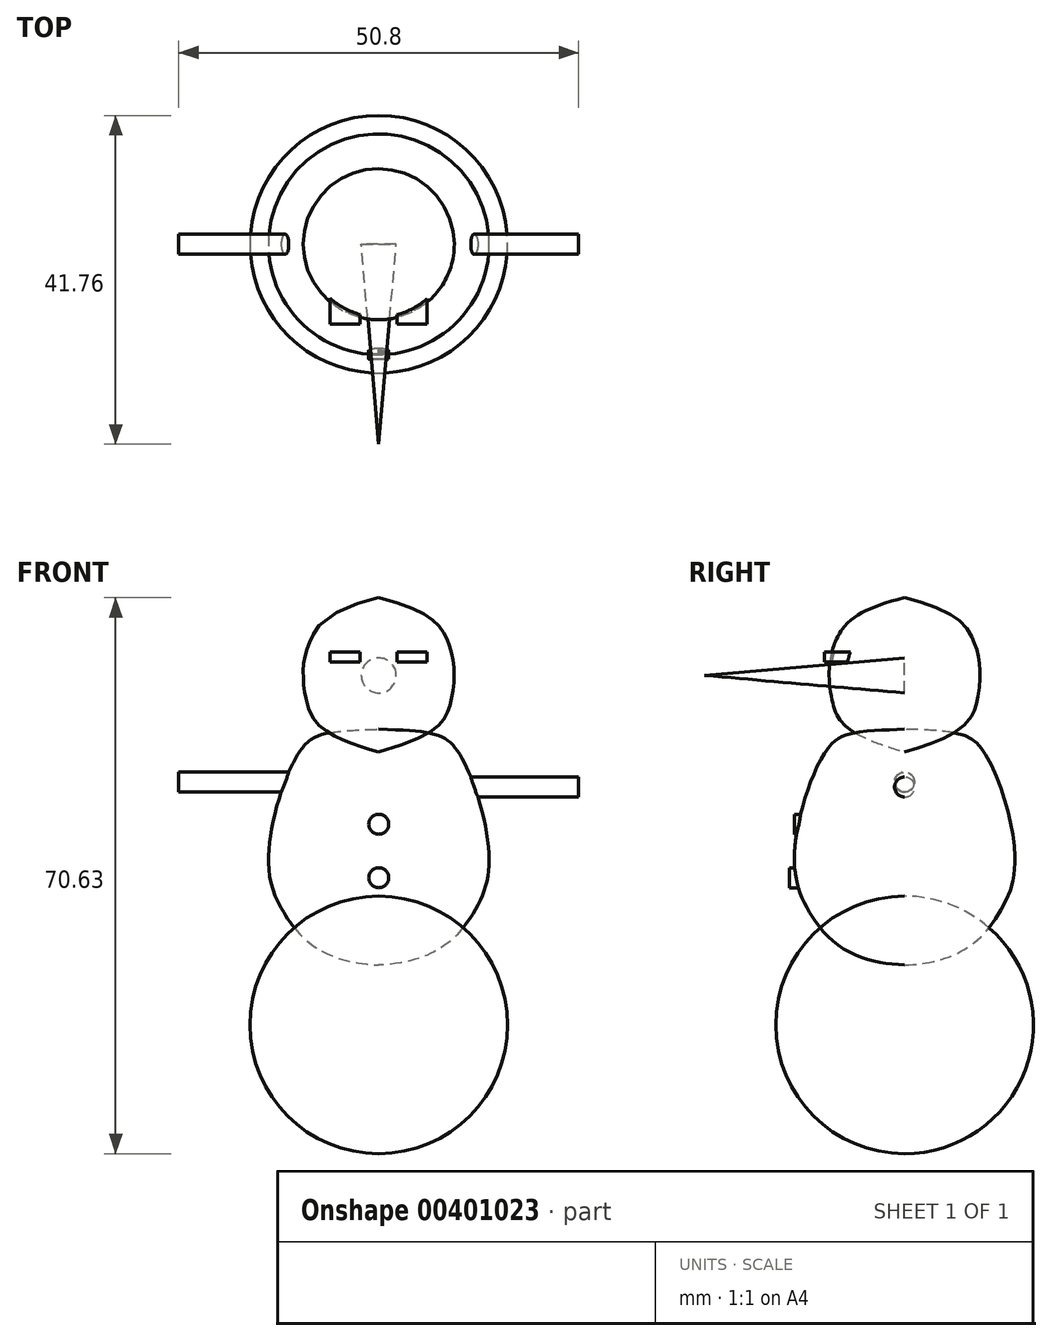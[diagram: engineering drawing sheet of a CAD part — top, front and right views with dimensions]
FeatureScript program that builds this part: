
annotation { "Feature Type Name" : "Feature", "Feature Type Description" : "" }
export const myFeature = defineFeature(function(context is Context, id is Id, definition is map)
    precondition{}
    {
        {
            var Q0;
            Q0=qCreatedBy(makeId("Front.planeOp"),FACE);
            var sketch = newSketch(context, id + "F0", { "sketchPlane" : qUnion([Q0])});
            skFitSpline(sketch, "E0", {"points": [v(0, 2.89) * mm, v(10.07, 0) * mm, v(14, -12.83) * mm, v(12.03, -20.44) * mm, v(0, -27.07) * mm], "startDerivative": vector(82.95, -3.07) * mm, "endDerivative": vector(-79.02, -2.93) * mm});
            skLineSegment(sketch, "E1", {"start": v(0, 54.46) * mm, "end": v(0, -50.15) * mm});
            skSolve(sketch);
        }
        {
            var Q0;
            {var subQ0=sQuery(id+"F0.wireOp",EDGE,"E0");Q0=makeQuery(id+"F0.imprint","IMPRINT",FACE,{"disambiguationData":[TD([[makeQuery(id+"F0.imprint","IMPRINT",EDGE,{"derivedFrom":subQ0}),-1.0]])]});}
            var Q1;
            Q1=sQuery(id+"F0.wireOp",EDGE,"E1");
            revolve(context, id + "F1", {"entities" : qUnion([Q0]), "axis" : qUnion([Q1]), "revolveType" : RevolveType.FULL});
        }
        {
            var Q0;
            Q0=qCreatedBy(makeId("Front.planeOp"),FACE);
            var sketch = newSketch(context, id + "F2", { "sketchPlane" : qUnion([Q0])});
            skLineSegment(sketch, "E2", {"start": v(0, 95.14) * mm, "end": v(0, -94.77) * mm});
            skFitSpline(sketch, "E3", {"points": [v(0, 19.59) * mm, v(8.6, 14.43) * mm, v(9.58, 10.5) * mm, v(9.09, 6.08) * mm, v(0, 0) * mm], "startDerivative": vector(61.63, -14.8) * mm, "endDerivative": vector(-73.17, -20.68) * mm});
            skSolve(sketch);
        }
        {
            var Q0;
            {var subQ0=sQuery(id+"F2.wireOp",EDGE,"E3");Q0=makeQuery(id+"F2.imprint","IMPRINT",FACE,{"disambiguationData":[TD([[makeQuery(id+"F2.imprint","IMPRINT",EDGE,{"derivedFrom":subQ0}),-1.0]])]});}
            var Q1;
            Q1=sQuery(id+"F2.wireOp",EDGE,"E2");
            revolve(context, id + "F3", {"entities" : qUnion([Q0]), "axis" : qUnion([Q1]), "revolveType" : RevolveType.FULL});
        }
        {
            var Q0;
            Q0=qCreatedBy(makeId("Front.planeOp"),FACE);
            var sketch = newSketch(context, id + "F4", { "sketchPlane" : qUnion([Q0])});
            skLineSegment(sketch, "E4", {"start": v(0, 39.72) * mm, "end": v(0, -72.26) * mm});
            skArc(sketch, "E5", {"start": v(0, -51.04) * mm, "mid": v(16.36, -34.68) * mm, "end": v(0, -18.33) * mm});
            skSolve(sketch);
        }
        {
            var Q0;
            {var subQ0=sQuery(id+"F4.wireOp",EDGE,"e939705f-58e8-430a-9148-d6e31caf1298");var subQ1=sQuery(id+"F4.wireOp",EDGE,"E4");var subQ2=makeQuery(id+"F4.imprint","INTERSECT",VERTEX,{"disambiguationData":[OD(0.0)],"derivedFrom":[subQ1,subQ0]});Q0=makeQuery(id+"F4.imprint","IMPRINT",FACE,{"disambiguationData":[TD([[makeQuery(id+"F4.imprint","IMPRINT",EDGE,{"disambiguationData":[TD([[subQ2,-1.0]])],"derivedFrom":subQ1}),1.0]])]});}
            var Q1;
            {var subQ0=sQuery(id+"F4.wireOp",EDGE,"E5");Q1=makeQuery(id+"F4.imprint","IMPRINT",FACE,{"disambiguationData":[TD([[makeQuery(id+"F4.imprint","IMPRINT",EDGE,{"derivedFrom":subQ0}),1.0]])]});}
            var Q2;
            Q2=sQuery(id+"F4.wireOp",EDGE,"E4");
            revolve(context, id + "F5", {"entities" : qUnion([Q0, Q1]), "axis" : qUnion([Q2]), "revolveType" : RevolveType.FULL});
        }
        {
            var Q0;
            Q0=qCreatedBy(makeId("Front.planeOp"),FACE);
            var sketch = newSketch(context, id + "F6", { "sketchPlane" : qUnion([Q0])});
            skLineSegment(sketch, "E6.bottom", {"start": v(-6.17, 12.7) * mm, "end": v(-2.36, 12.7) * mm});
            skLineSegment(sketch, "E6.top", {"start": v(-6.17, 11.43) * mm, "end": v(-2.36, 11.43) * mm});
            skLineSegment(sketch, "E6.left", {"start": v(-6.17, 12.7) * mm, "end": v(-6.17, 11.43) * mm});
            skLineSegment(sketch, "E6.right", {"start": v(-2.36, 12.7) * mm, "end": v(-2.36, 11.43) * mm});
            skSolve(sketch);
        }
        {
            var Q0;
            Q0 = qSketchRegion(id + "F6", true);
            extrude(context, id + "F7", {"entities" : qUnion([Q0]), "operationType" : NewBodyOperationType.ADD, "depth" : 10.16 * mm});
        }
        {
            var Q0;
            Q0=qCreatedBy(makeId("Front.planeOp"),FACE);
            var sketch = newSketch(context, id + "F8", { "sketchPlane" : qUnion([Q0])});
            skLineSegment(sketch, "E7.bottom", {"start": v(2.34, 12.67) * mm, "end": v(6.15, 12.67) * mm});
            skLineSegment(sketch, "E7.top", {"start": v(2.34, 11.4) * mm, "end": v(6.15, 11.4) * mm});
            skLineSegment(sketch, "E7.left", {"start": v(2.34, 12.67) * mm, "end": v(2.34, 11.4) * mm});
            skLineSegment(sketch, "E7.right", {"start": v(6.15, 12.67) * mm, "end": v(6.15, 11.4) * mm});
            skSolve(sketch);
        }
        {
            var Q0;
            Q0 = qSketchRegion(id + "F8", true);
            extrude(context, id + "F9", {"entities" : qUnion([Q0]), "operationType" : NewBodyOperationType.ADD, "depth" : 10.16 * mm});
        }
        {
            var Q0;
            Q0=qCreatedBy(makeId("Front.planeOp"),FACE);
            var sketch = newSketch(context, id + "F10", { "sketchPlane" : qUnion([Q0])});
            skCircle(sketch, "E8", {"center": v(0, 9.71) * mm, "radius": 2.22 * mm});
            skSolve(sketch);
        }
        {
            var Q0;
            Q0 = qSketchRegion(id + "F10", true);
            extrude(context, id + "F11", {"entities" : qUnion([Q0]), "depth" : 27.13 * mm, "hasDraft" : true, "draftAngle" : 5 * degree, "draftPullDirection" : true});
        }
        {
            var Q0;
            Q0=qCreatedBy(makeId("Right.planeOp"),FACE);
            var sketch = newSketch(context, id + "F12", { "sketchPlane" : qUnion([Q0])});
            skCircle(sketch, "E9", {"center": v(0, -4.47) * mm, "radius": 1.27 * mm});
            skSolve(sketch);
        }
        {
            var Q0;
            Q0 = qSketchRegion(id + "F12", true);
            var Q1;
            Q1 = qSketchRegion(id + "F14", true);
            extrude(context, id + "F13", {"entities" : qUnion([Q0, Q1]), "operationType" : NewBodyOperationType.ADD, "depth" : 25.4 * mm});
        }
        {
            var Q0;
            Q0=qCreatedBy(makeId("Right.planeOp"),FACE);
            var sketch = newSketch(context, id + "F14", { "sketchPlane" : qUnion([Q0])});
            skCircle(sketch, "E10", {"center": v(0, -3.85) * mm, "radius": 1.27 * mm});
            skSolve(sketch);
        }
        {
            var Q0;
            Q0 = qSketchRegion(id + "F14", true);
            extrude(context, id + "F15", {"entities" : qUnion([Q0]), "operationType" : NewBodyOperationType.ADD, "oppositeDirection" : true, "depth" : 25.4 * mm});
        }
        {
            var Q0;
            Q0=qCreatedBy(makeId("Front.planeOp"),FACE);
            var sketch = newSketch(context, id + "F16", { "sketchPlane" : qUnion([Q0])});
            skCircle(sketch, "E11", {"center": v(0, -9.19) * mm, "radius": 1.27 * mm});
            skSolve(sketch);
        }
        {
            var Q0;
            Q0 = qSketchRegion(id + "F16", true);
            extrude(context, id + "F17", {"entities" : qUnion([Q0]), "operationType" : NewBodyOperationType.ADD, "depth" : 13.97 * mm});
        }
        {
            var Q0;
            Q0=qCreatedBy(makeId("Front.planeOp"),FACE);
            var sketch = newSketch(context, id + "F18", { "sketchPlane" : qUnion([Q0])});
            skCircle(sketch, "E12", {"center": v(0, -15.99) * mm, "radius": 1.27 * mm});
            skSolve(sketch);
        }
        {
            var Q0;
            Q0 = qSketchRegion(id + "F18", true);
            extrude(context, id + "F19", {"entities" : qUnion([Q0]), "operationType" : NewBodyOperationType.ADD, "depth" : 14.6 * mm});
        }
    });
